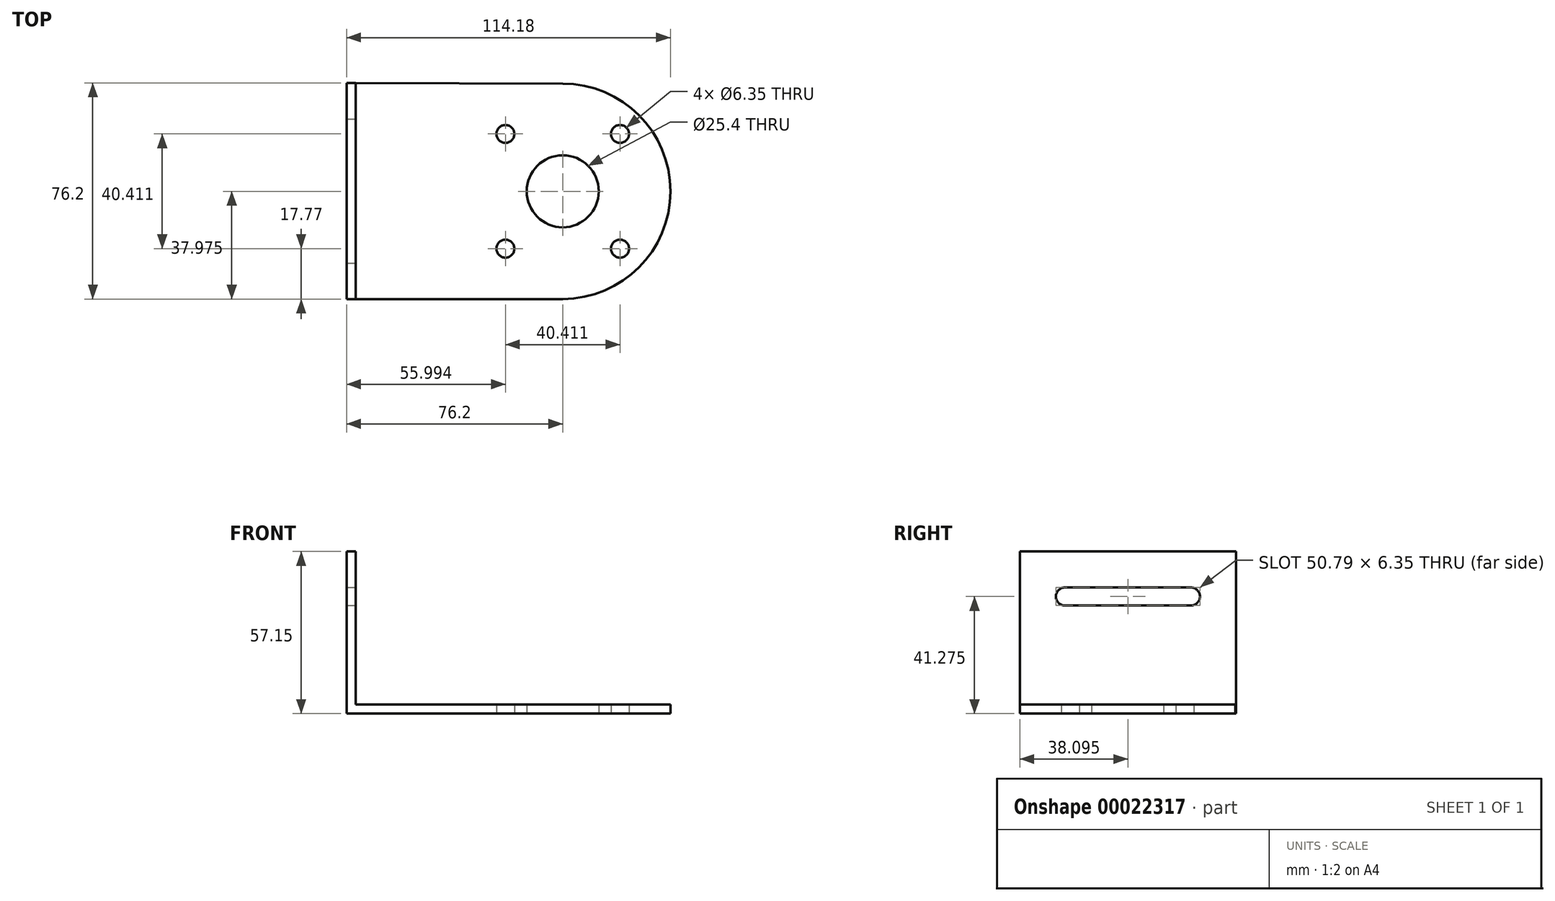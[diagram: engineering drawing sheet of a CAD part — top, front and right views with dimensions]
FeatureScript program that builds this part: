
annotation { "Feature Type Name" : "Feature", "Feature Type Description" : "" }
export const myFeature = defineFeature(function(context is Context, id is Id, definition is map)
    precondition{}
    {
        {
            var Q0;
            Q0=qCreatedBy(makeId("Top.planeOp"),FACE);
            var sketch = newSketch(context, id + "F0", { "sketchPlane" : qUnion([Q0])});
            skCircle(sketch, "E0", {"center": v(56, 58.18) * mm, "radius": 3.18 * mm});
            skCircle(sketch, "E1.1.0", {"center": v(56, 17.77) * mm, "radius": 3.18 * mm});
            skCircle(sketch, "E1.2.0", {"center": v(96.4, 17.77) * mm, "radius": 3.18 * mm});
            skCircle(sketch, "E1.3.0", {"center": v(96.4, 58.18) * mm, "radius": 3.18 * mm});
            skPoint(sketch, "E1.center", {"position": v(76.2, 37.98) * mm});
            skCircle(sketch, "E2", {"center": v(76.2, 37.98) * mm, "radius": 12.7 * mm});
            skLineSegment(sketch, "E3", {"start": v(0, 0) * mm, "end": v(76.2, 0) * mm});
            skArc(sketch, "E4", {"start": v(76.2, 0) * mm, "mid": v(114.18, 37.98) * mm, "end": v(76.2, 75.95) * mm});
            skLineSegment(sketch, "E5", {"start": v(76.2, 75.95) * mm, "end": v(0, 76.2) * mm});
            skLineSegment(sketch, "E6", {"start": v(0, 76.2) * mm, "end": v(0, 0) * mm});
            skSolve(sketch);
        }
        {
            var Q0;
            Q0=makeQuery(id+"F0.imprint","IMPRINT",FACE,{"disambiguationData":[TD([[makeQuery(id+"F0.imprint","IMPRINT",EDGE,{"derivedFrom":sQuery(id+"F0.wireOp",EDGE,"E0")}),-1.0]])]});
            extrude(context, id + "F1", {"entities" : qUnion([Q0]), "depth" : 3.17 * mm});
        }
        {
            var Q0;
            Q0=makeQuery(id+"F1.opExtrude","CAP_FACE",FACE,{"disambiguationData":[OSD([sQuery(id+"F0.wireOp",EDGE,"E0"),sQuery(id+"F0.wireOp",EDGE,"E1.1.0"),sQuery(id+"F0.wireOp",EDGE,"E1.2.0"),sQuery(id+"F0.wireOp",EDGE,"E1.3.0"),sQuery(id+"F0.wireOp",EDGE,"E2"),sQuery(id+"F0.wireOp",EDGE,"E3"),sQuery(id+"F0.wireOp",EDGE,"E4"),sQuery(id+"F0.wireOp",EDGE,"E5"),sQuery(id+"F0.wireOp",EDGE,"E6")])],"isStart":false});
            var sketch = newSketch(context, id + "F2", { "sketchPlane" : qUnion([Q0])});
            skLineSegment(sketch, "E7", {"start": v(3.18, 76.19) * mm, "end": v(3.18, 0) * mm});
            skLineSegment(sketch, "E8", {"start": v(0, 0) * mm, "end": v(60.6, 0) * mm});
            skSolve(sketch);
        }
        {
            var Q0;
            {var subQ1=sQuery(id+"F2.wireOp",EDGE,"E7");Q0=makeQuery(id+"F2.imprint","IMPRINT",FACE,{"disambiguationData":[TD([[makeQuery(id+"F2.imprint","IMPRINT",EDGE,{"derivedFrom":subQ1}),-1.0]])]});}
            extrude(context, id + "F3", {"entities" : qUnion([Q0]), "operationType" : NewBodyOperationType.ADD, "depth" : 53.97 * mm});
        }
        {
            var Q0;
            Q0=makeQuery(id+"F3.opExtrude","SWEPT_FACE",FACE,{"disambiguationData":[OSD([sQuery(id+"F2.wireOp",EDGE,"E7")])]});
            var sketch = newSketch(context, id + "F4", { "sketchPlane" : qUnion([Q0])});
            skArc(sketch, "E9", {"start": v(15.87, 44.45) * mm, "mid": v(12.7, 41.27) * mm, "end": v(15.88, 38.1) * mm});
            skArc(sketch, "E10", {"start": v(60.33, 38.1) * mm, "mid": v(63.49, 41.28) * mm, "end": v(60.32, 44.45) * mm});
            skLineSegment(sketch, "E11", {"start": v(15.87, 44.45) * mm, "end": v(60.32, 44.45) * mm});
            skLineSegment(sketch, "E12", {"start": v(15.88, 38.1) * mm, "end": v(60.33, 38.1) * mm});
            skSolve(sketch);
        }
        {
            var Q0;
            Q0=makeQuery(id+"F4.imprint","IMPRINT",FACE,{"disambiguationData":[TD([[makeQuery(id+"F4.imprint","IMPRINT",EDGE,{"derivedFrom":sQuery(id+"F4.wireOp",EDGE,"E9")}),1.0]])]});
            extrude(context, id + "F5", {"entities" : qUnion([Q0]), "operationType" : NewBodyOperationType.REMOVE, "endBound" : BoundingType.UP_TO_NEXT, "oppositeDirection" : true, "depth" : 24.33 * mm});
        }
    });
